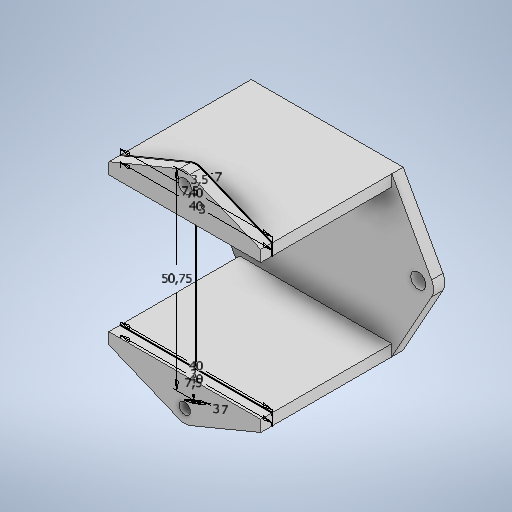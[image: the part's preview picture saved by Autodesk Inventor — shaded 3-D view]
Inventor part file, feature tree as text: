
AUTODESK INVENTOR PART (.ipt)
format: ipt  version: 2025.2 (Build 292293000, 293)  size: 284,160 bytes
history: native  units: mm
features: extrude x3, sketch x2
ambient origin geometry x8: Origin, YZ Plane, XZ Plane, XY Plane, X Axis, Y Axis, Z Axis, Center Point
bodies: Solid1 (feature_tree)
feature tree (5):
  sketch  "Sketch1"  dims[d0=3.5mm d1=50.75mm]
  extrude  "Extrusion1"  Depth=50.75mm
  extrude  "Extrusion2"  Depth=3.0mm
  extrude  "Extrusion3"  Depth=3.0mm
  sketch  "Sketch2"  dims[d2=3.0mm d3=7.5mm d4=3.0mm d5=40.0mm d6=40.0mm d7=7.0mm d8=7.5mm d9=3.0mm d10=40.0mm d11=40.0mm d12=7.0mm d13=3.0mm d14=0.0mm d15=31.5mm d16=0.0mm d17=17.875mm d18=54.0mm d19=8.0mm d20=4.0mm d21=8.0mm d22=4.0mm d23=3.0mm d24=0.0mm]
